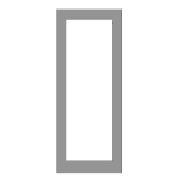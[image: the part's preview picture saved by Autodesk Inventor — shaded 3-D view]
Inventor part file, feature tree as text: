
AUTODESK INVENTOR PART (.ipt)
format: ipt  version: 2022.2 (Build 262287000, 287)  size: 177,664 bytes
history: native  units: in
note: dims shown in document units (in); Inventor stores cm internally (conversion verified against a paired STEP export)
features: sketch x9, other x4, hole x3, plane x1
ambient origin geometry x8: Origin, YZ Plane, XZ Plane, XY Plane, X Axis, Y Axis, Z Axis, Center Point
bodies: Solid1 (feature_tree), Body (feature_tree)
feature tree (17):
  other  "Driven Length"
  other  "Frame Generator"
  other  "Start Plane"
  other  "End Plane"
  sketch  "Sketch9"  dims[d6=-0.0in d7=20.0in]
  sketch  "Sketch10"  dims[d8=0.13in d9=0.0in]
  hole  "Hole2"  [1 undecoded]
  sketch  "Sketch12"  dims[d11=20.0in]
  hole  "Hole3"  [1 undecoded]
  hole  "Hole4"  [1 undecoded]
  sketch  "Sketch"  dims[d25=1.0in d26=0.5in d27=0.5in d28=0.25in d29=1.0in d30=1.0in d31=0.1695in d32=0.75in d33=0.375in d34=0.25in d35=0.5635in d36=2.0in d37=0.8108in d38=3.5in d39=3.5in d40=0.375in d41=1.25in d42=0.257in d43=0.75in d44=0.375in d45=0.06in d46=0.5635in d47=2.0in d48=0.8108in d49=0.375in d50=1.25in d51=3.5in d52=3.5in d53=0.257in d54=0.75in d55=0.375in d56=0.25in d57=0.5635in d58=2.0in d59=0.8108in d60=1.0in d61=1.0in d62=1.0in d63=0.15in d64=0.25in d65=0.375in d66=0.5635in d67=0.75in d68=0.8108in d69=0.0625in d70=0.75in d71=0.375in]
  sketch  "Sketch6"  dims[d0=1.0in d1=2.0in]
  plane  "Work Plane5"
  sketch  "Sketch7"  dims[d2=0.125in d3=0.125in]
  sketch  "Sketch11"  dims[d14=90.0deg]
  sketch  "Sketch13"  dims[d23=0.5in]
  sketch  "Sketch14"  dims[d24=1.0in]
note: 3 required parameter values undecoded (feature->parameter linkage not recoverable at this tier; creation-order binding heuristic only, values carry confidence <= 0.55)
